# Revit family: Sanitary_Basins_Cosentino_Reflection1
name_source: partatom
category: Plumbing Fixtures
units: mm (PartAtom-declared; Revit-internal decimal feet)

## family parameters
Always vertical = Yes
Cut with Voids When Loaded = No
Host = Wall
Part Type = Normal
Room Calculation Point = No
Round Connector Dimension = Use Diameter
Shared = No

## types (1)
- Basin 490mm
    Assembly Code = D2010400
    CW Connection = No
    Default Elevation = 0 mm  [stored 0 ft]
    Description = The basin is one of the stars of your bathroom. Cosentino offers unique designs which fit smoothly into your room, your style, and the needs of your family.

Whether it’s for a master bathroom or a downstairs WC, we have the perfect product to transform your bathroom into a warm, welcoming space.
    Edition number = 1
    HW Connection = No
    Keynote = 10800
    Manufacturer = Cosentino
    Model = Reflection
    Product Guid = 3421ddd4-7f32-44d3-8549-346075c5a552
    Product Material = Natural Stone - Cosentino - Dekton - Vapour - Matt
    Product data url = https://www.bimobject.com
    URL = www.cosentino.com
    Vent Connection = No
    Ι_Dstnc = 490 mm  [stored 1.60761 ft]
    Ι_Typ Ntgr = 1

note: [stored X ft] marks values corroborated as IEEE doubles in the binary element streams (Revit-internal decimal feet)

## geometry (parser evidence)
native form markers: Sweep x2
no freeform markers — native parametric forms only
